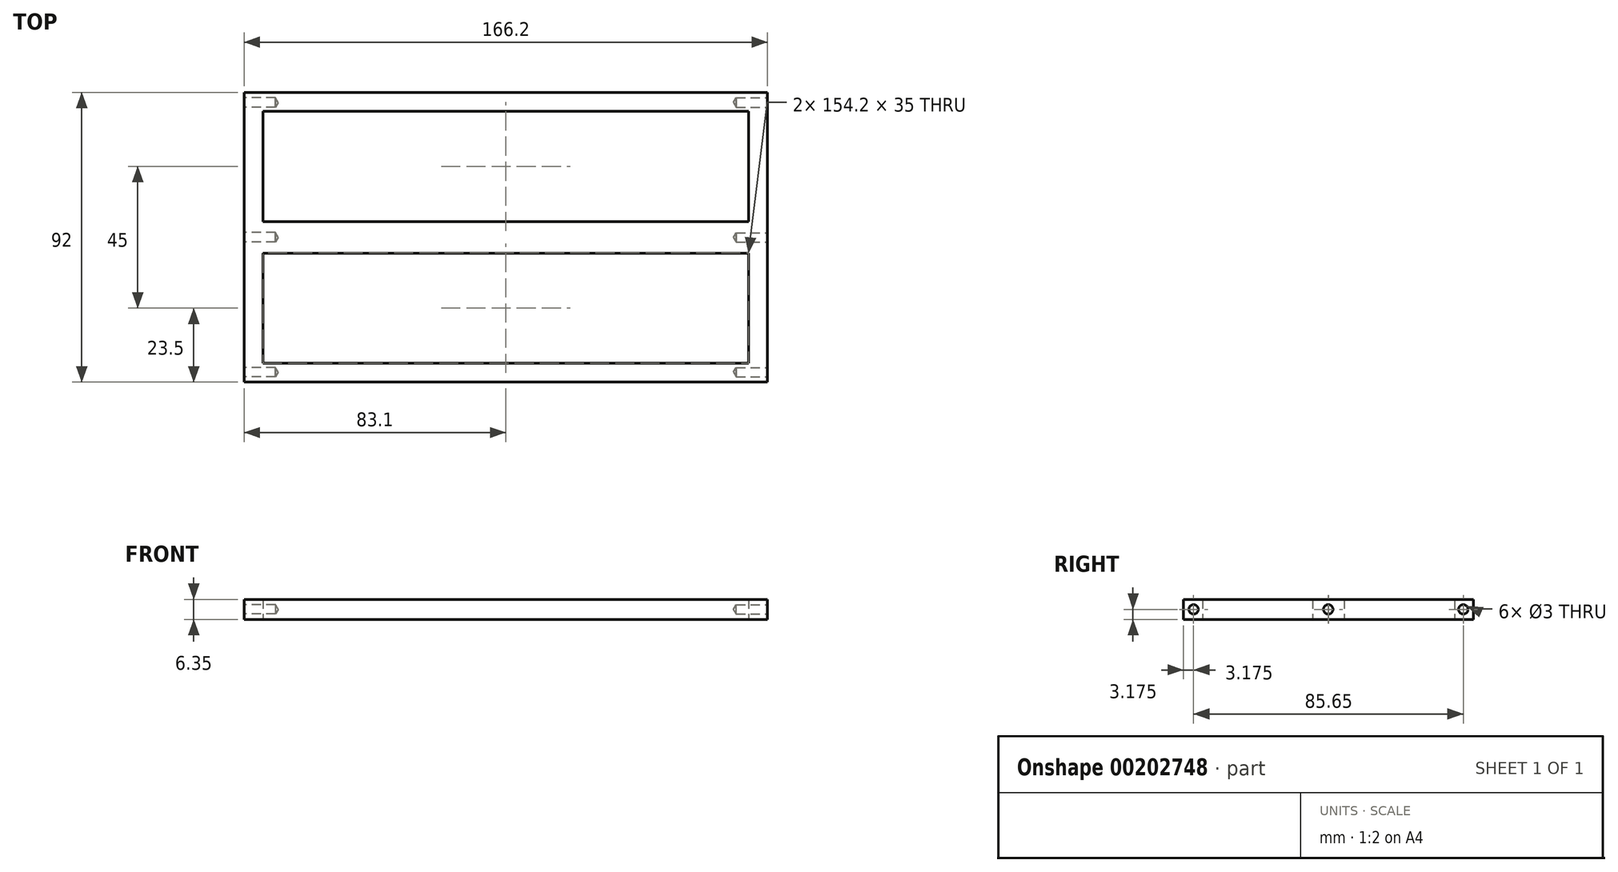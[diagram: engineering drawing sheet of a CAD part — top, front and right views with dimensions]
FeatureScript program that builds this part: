
annotation { "Feature Type Name" : "Feature", "Feature Type Description" : "" }
export const myFeature = defineFeature(function(context is Context, id is Id, definition is map)
    precondition{}
    {
        {
            var Q0;
            Q0=qCreatedBy(makeId("Top.planeOp"),FACE);
            var sketch = newSketch(context, id + "F0", { "sketchPlane" : qUnion([Q0])});
            skLineSegment(sketch, "E0.bottom", {"start": v(83.1, -46) * mm, "end": v(-83.1, -46) * mm});
            skLineSegment(sketch, "E0.top", {"start": v(83.1, 46) * mm, "end": v(-83.1, 46) * mm});
            skLineSegment(sketch, "E0.left", {"start": v(83.1, -46) * mm, "end": v(83.1, 46) * mm});
            skLineSegment(sketch, "E0.right", {"start": v(-83.1, -46) * mm, "end": v(-83.1, 46) * mm});
            skPoint(sketch, "E0.middle", {"position": v(0, 0) * mm});
            skLineSegment(sketch, "E1.bottom", {"start": v(83.1, -5) * mm, "end": v(-83.1, -5) * mm});
            skLineSegment(sketch, "E1.top", {"start": v(83.1, 5) * mm, "end": v(-83.1, 5) * mm});
            skLineSegment(sketch, "E1.left", {"start": v(83.1, -5) * mm, "end": v(83.1, 5) * mm});
            skLineSegment(sketch, "E1.right", {"start": v(-83.1, -5) * mm, "end": v(-83.1, 5) * mm});
            skLineSegment(sketch, "E2", {"start": v(-83.1, 40) * mm, "end": v(83.1, 40) * mm});
            skLineSegment(sketch, "E3", {"start": v(-83.1, -40) * mm, "end": v(83.1, -40) * mm});
            skLineSegment(sketch, "E4", {"start": v(-77.1, 46) * mm, "end": v(-77.1, -46) * mm});
            skLineSegment(sketch, "E5", {"start": v(77.1, 46) * mm, "end": v(77.1, -46) * mm});
            skPoint(sketch, "E6", {"position": v(-83.1, -3) * mm});
            skPoint(sketch, "E7", {"position": v(83.1, -3) * mm});
            skPoint(sketch, "E8", {"position": v(-83.1, 3) * mm});
            skPoint(sketch, "E9", {"position": v(83.1, 3) * mm});
            skSolve(sketch);
        }
        {
            var Q0;
            {var subQ0=sQuery(id+"F0.wireOp",EDGE,"E0.bottom");Q0=makeQuery(id+"F0.imprint","IMPRINT",FACE,{"disambiguationData":[TD([[makeQuery(id+"F0.imprint","IMPRINT",EDGE,{"derivedFrom":subQ0}),-1.0]])]});}
            var Q1;
            {var subQ0=sQuery(id+"F0.wireOp",EDGE,"E0.top");Q1=makeQuery(id+"F0.imprint","IMPRINT",FACE,{"disambiguationData":[TD([[makeQuery(id+"F0.imprint","IMPRINT",EDGE,{"derivedFrom":subQ0}),1.0]])]});}
            var Q2;
            Q2=makeQuery(id+"F0.imprint","IMPRINT",FACE,{"disambiguationData":[TD([[makeQuery(id+"F0.imprint","IMPRINT",EDGE,{"derivedFrom":sQuery(id+"F0.wireOp",EDGE,"E1.bottom")}),-1.0]])]});
            var Q3;
            {var subQ1=sQuery(id+"F0.wireOp",EDGE,"E0.right");var subQ3=sQuery(id+"F0.wireOp",EDGE,"E2");var subQ4=makeQuery(id+"F0.imprint","INTERSECT",VERTEX,{"derivedFrom":[subQ1,subQ3]});Q3=makeQuery(id+"F0.imprint","IMPRINT",FACE,{"disambiguationData":[TD([[makeQuery(id+"F0.imprint","IMPRINT",EDGE,{"disambiguationData":[TD([[subQ4,-1.0]])],"derivedFrom":subQ3}),-1.0]])]});}
            var Q4;
            {var subQ1=sQuery(id+"F0.wireOp",EDGE,"E0.right");var subQ3=sQuery(id+"F0.wireOp",EDGE,"E3");var subQ4=makeQuery(id+"F0.imprint","INTERSECT",VERTEX,{"derivedFrom":[subQ1,subQ3]});Q4=makeQuery(id+"F0.imprint","IMPRINT",FACE,{"disambiguationData":[TD([[makeQuery(id+"F0.imprint","IMPRINT",EDGE,{"disambiguationData":[TD([[subQ4,-1.0]])],"derivedFrom":subQ3}),1.0]])]});}
            var Q5;
            {var subQ1=sQuery(id+"F0.wireOp",EDGE,"E0.left");var subQ3=sQuery(id+"F0.wireOp",EDGE,"E2");var subQ4=makeQuery(id+"F0.imprint","INTERSECT",VERTEX,{"derivedFrom":[subQ1,subQ3]});Q5=makeQuery(id+"F0.imprint","IMPRINT",FACE,{"disambiguationData":[TD([[makeQuery(id+"F0.imprint","IMPRINT",EDGE,{"disambiguationData":[TD([[subQ4,1.0]])],"derivedFrom":subQ3}),-1.0]])]});}
            var Q6;
            {var subQ1=sQuery(id+"F0.wireOp",EDGE,"E0.left");var subQ3=sQuery(id+"F0.wireOp",EDGE,"E3");var subQ4=makeQuery(id+"F0.imprint","INTERSECT",VERTEX,{"derivedFrom":[subQ1,subQ3]});Q6=makeQuery(id+"F0.imprint","IMPRINT",FACE,{"disambiguationData":[TD([[makeQuery(id+"F0.imprint","IMPRINT",EDGE,{"disambiguationData":[TD([[subQ4,1.0]])],"derivedFrom":subQ3}),1.0]])]});}
            extrude(context, id + "F1", {"entities" : qUnion([Q0, Q1, Q2, Q3, Q4, Q5, Q6]), "depth" : 6.35 * mm});
        }
        {
            var Q0;
            Q0=makeQuery(id+"F1.opExtrude","SWEPT_FACE",FACE,{"disambiguationData":[OSD([sQuery(id+"F0.wireOp",EDGE,"E0.right"),sQuery(id+"F0.wireOp",EDGE,"E1.right")])]});
            var sketch = newSketch(context, id + "F2", { "sketchPlane" : qUnion([Q0])});
            skLineSegment(sketch, "E10.bottom", {"start": v(-46, 6.35) * mm, "end": v(-39.65, 6.35) * mm});
            skLineSegment(sketch, "E10.top", {"start": v(-46, 0) * mm, "end": v(-39.65, 0) * mm});
            skLineSegment(sketch, "E10.left", {"start": v(-46, 6.35) * mm, "end": v(-46, 0) * mm});
            skLineSegment(sketch, "E10.right", {"start": v(-39.65, 6.35) * mm, "end": v(-39.65, 0) * mm});
            skLineSegment(sketch, "E11.bottom", {"start": v(46, 6.35) * mm, "end": v(39.65, 6.35) * mm});
            skLineSegment(sketch, "E11.top", {"start": v(46, 0) * mm, "end": v(39.65, 0) * mm});
            skLineSegment(sketch, "E11.left", {"start": v(46, 6.35) * mm, "end": v(46, 0) * mm});
            skLineSegment(sketch, "E11.right", {"start": v(39.65, 6.35) * mm, "end": v(39.65, 0) * mm});
            skPoint(sketch, "E12", {"position": v(42.83, 3.17) * mm});
            skLineSegment(sketch, "E13.bottom", {"start": v(3.17, 0) * mm, "end": v(-3.18, 0) * mm});
            skLineSegment(sketch, "E13.top", {"start": v(3.17, 6.35) * mm, "end": v(-3.17, 6.35) * mm});
            skLineSegment(sketch, "E13.left", {"start": v(3.17, 0) * mm, "end": v(3.17, 6.35) * mm});
            skLineSegment(sketch, "E13.right", {"start": v(-3.18, 0) * mm, "end": v(-3.17, 6.35) * mm});
            skPoint(sketch, "E13.middle", {"position": v(0, 3.18) * mm});
            skPoint(sketch, "E14", {"position": v(-42.83, 3.17) * mm});
            skSolve(sketch);
        }
        {
            var Q0;
            Q0=sQuery(id+"F2.wireOp",VERTEX,"E14");
            var Q1;
            Q1=sQuery(id+"F2.wireOp",VERTEX,"E13.middle");
            var Q2;
            Q2=sQuery(id+"F2.wireOp",VERTEX,"E12");
            var Q3;
            Q3=makeQuery(id+"F1.opExtrude","SWEPT_BODY",BODY,{"disambiguationData":[OSD([sQuery(id+"F0.wireOp",EDGE,"E0.bottom"),sQuery(id+"F0.wireOp",EDGE,"E0.top"),sQuery(id+"F0.wireOp",EDGE,"E0.left"),sQuery(id+"F0.wireOp",EDGE,"E0.right"),sQuery(id+"F0.wireOp",EDGE,"E1.bottom"),sQuery(id+"F0.wireOp",EDGE,"E1.top"),sQuery(id+"F0.wireOp",EDGE,"E1.left"),sQuery(id+"F0.wireOp",EDGE,"E1.right"),sQuery(id+"F0.wireOp",EDGE,"E2"),sQuery(id+"F0.wireOp",EDGE,"E3"),sQuery(id+"F0.wireOp",EDGE,"E4"),sQuery(id+"F0.wireOp",EDGE,"E5")])]});
            hole(context, id + "F3", {"style" : HoleStyle.SIMPLE, "endStyle" : HoleEndStyle.BLIND, "standardTappedOrClearance" : lookupTablePath({ "standard" : "ISO", "size" : "3", "type" : "Drilled" }), "standardBlindInLast" : lookupTablePath({ "standard" : "ISO", "size" : "3", "type" : "Drilled" }), "holeDiameter" : 3 * mm, "holeDepth" : 10 * mm, "startFromSketch" : true, "locations" : qUnion([Q0, Q1, Q2]), "scope" : qUnion([Q3])});
        }
        {
            var Q0;
            Q0=makeQuery(id+"F1.opExtrude","SWEPT_FACE",FACE,{"disambiguationData":[OSD([sQuery(id+"F0.wireOp",EDGE,"E0.left"),sQuery(id+"F0.wireOp",EDGE,"E1.left")])]});
            var sketch = newSketch(context, id + "F4", { "sketchPlane" : qUnion([Q0])});
            skLineSegment(sketch, "E15.bottom", {"start": v(-46, 6.35) * mm, "end": v(-39.65, 6.35) * mm});
            skLineSegment(sketch, "E15.top", {"start": v(-46, 0) * mm, "end": v(-39.65, 0) * mm});
            skLineSegment(sketch, "E15.left", {"start": v(-46, 6.35) * mm, "end": v(-46, 0) * mm});
            skLineSegment(sketch, "E15.right", {"start": v(-39.65, 6.35) * mm, "end": v(-39.65, 0) * mm});
            skPoint(sketch, "E16", {"position": v(-42.83, 3.17) * mm});
            skPoint(sketch, "E16.positionSnap0", {"position": v(-46, 3.17) * mm});
            skPoint(sketch, "E16.positionSnap1", {"position": v(-42.83, 6.35) * mm});
            skLineSegment(sketch, "E17.bottom", {"start": v(46, 6.35) * mm, "end": v(39.65, 6.35) * mm});
            skLineSegment(sketch, "E17.top", {"start": v(46, 0) * mm, "end": v(39.65, 0) * mm});
            skLineSegment(sketch, "E17.left", {"start": v(46, 6.35) * mm, "end": v(46, 0) * mm});
            skLineSegment(sketch, "E17.right", {"start": v(39.65, 6.35) * mm, "end": v(39.65, 0) * mm});
            skPoint(sketch, "E18", {"position": v(42.83, 3.17) * mm});
            skPoint(sketch, "E18.positionSnap0", {"position": v(39.65, 3.17) * mm});
            skPoint(sketch, "E18.positionSnap1", {"position": v(42.83, 6.35) * mm});
            skPoint(sketch, "E19", {"position": v(-0.06, 3.17) * mm});
            skLineSegment(sketch, "E20.bottom", {"start": v(3.11, 0) * mm, "end": v(-3.24, 0) * mm});
            skLineSegment(sketch, "E20.top", {"start": v(3.11, 6.35) * mm, "end": v(-3.24, 6.35) * mm});
            skLineSegment(sketch, "E20.left", {"start": v(3.11, 0) * mm, "end": v(3.11, 6.35) * mm});
            skLineSegment(sketch, "E20.right", {"start": v(-3.24, 0) * mm, "end": v(-3.24, 6.35) * mm});
            skSolve(sketch);
        }
        {
            var Q0;
            Q0=sQuery(id+"F4.wireOp",VERTEX,"E19");
            var Q1;
            Q1=sQuery(id+"F4.wireOp",VERTEX,"E16");
            var Q2;
            Q2=sQuery(id+"F4.wireOp",VERTEX,"E18");
            var Q3;
            Q3=makeQuery(id+"F1.opExtrude","SWEPT_BODY",BODY,{"disambiguationData":[OSD([sQuery(id+"F0.wireOp",EDGE,"E0.bottom"),sQuery(id+"F0.wireOp",EDGE,"E0.top"),sQuery(id+"F0.wireOp",EDGE,"E0.left"),sQuery(id+"F0.wireOp",EDGE,"E0.right"),sQuery(id+"F0.wireOp",EDGE,"E1.bottom"),sQuery(id+"F0.wireOp",EDGE,"E1.top"),sQuery(id+"F0.wireOp",EDGE,"E1.left"),sQuery(id+"F0.wireOp",EDGE,"E1.right"),sQuery(id+"F0.wireOp",EDGE,"E2"),sQuery(id+"F0.wireOp",EDGE,"E3"),sQuery(id+"F0.wireOp",EDGE,"E4"),sQuery(id+"F0.wireOp",EDGE,"E5")])]});
            hole(context, id + "F5", {"style" : HoleStyle.SIMPLE, "endStyle" : HoleEndStyle.BLIND, "standardTappedOrClearance" : lookupTablePath({ "standard" : "ISO", "size" : "3", "type" : "Drilled" }), "standardBlindInLast" : lookupTablePath({ "standard" : "ISO", "size" : "3", "type" : "Drilled" }), "holeDiameter" : 3 * mm, "holeDepth" : 10 * mm, "startFromSketch" : true, "locations" : qUnion([Q0, Q1, Q2]), "scope" : qUnion([Q3])});
        }
    });
